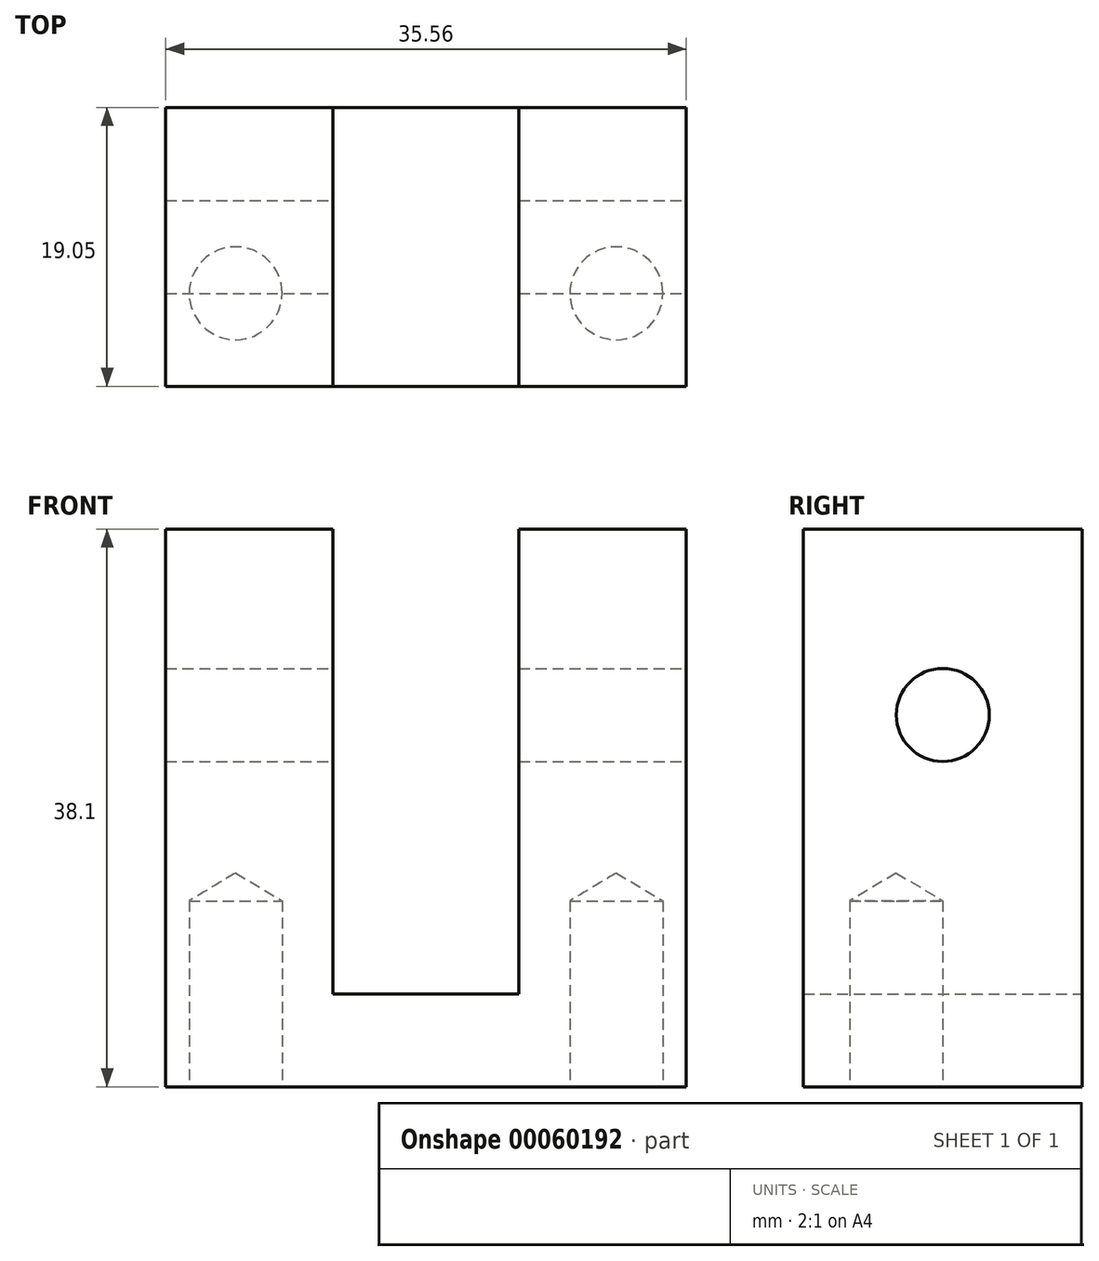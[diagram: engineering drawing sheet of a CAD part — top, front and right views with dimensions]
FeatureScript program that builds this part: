
annotation { "Feature Type Name" : "Feature", "Feature Type Description" : "" }
export const myFeature = defineFeature(function(context is Context, id is Id, definition is map)
    precondition{}
    {
        {
            var Q0;
            Q0=qCreatedBy(makeId("Front.planeOp"),FACE);
            var sketch = newSketch(context, id + "F0", { "sketchPlane" : qUnion([Q0])});
            skLineSegment(sketch, "E0", {"start": v(0, 54.37) * mm, "end": v(0, -36.21) * mm, "construction": true});
            skLineSegment(sketch, "E1", {"start": v(-17.78, -25.4) * mm, "end": v(17.78, -25.4) * mm});
            skLineSegment(sketch, "E2", {"start": v(17.78, -25.4) * mm, "end": v(17.78, 12.7) * mm});
            skLineSegment(sketch, "E3", {"start": v(17.78, 12.7) * mm, "end": v(6.35, 12.7) * mm});
            skLineSegment(sketch, "E4", {"start": v(6.35, 12.7) * mm, "end": v(6.35, -19.05) * mm});
            skLineSegment(sketch, "E5", {"start": v(6.35, -19.05) * mm, "end": v(-6.35, -19.05) * mm});
            skLineSegment(sketch, "E6", {"start": v(-6.35, -19.05) * mm, "end": v(-6.35, 12.7) * mm});
            skLineSegment(sketch, "E7", {"start": v(-6.35, 12.7) * mm, "end": v(-17.78, 12.7) * mm});
            skLineSegment(sketch, "E8", {"start": v(-17.78, 12.7) * mm, "end": v(-17.78, -25.4) * mm});
            skLineSegment(sketch, "E9", {"start": v(-40.6, 0) * mm, "end": v(30.07, 0) * mm, "construction": true});
            skSolve(sketch);
        }
        {
            var Q0;
            Q0 = qSketchRegion(id + "F0", true);
            extrude(context, id + "F1", {"entities" : qUnion([Q0]), "depth" : 19.05 * mm});
        }
        {
            var Q0;
            Q0=makeQuery(id+"F1.opExtrude","SWEPT_FACE",FACE,{"disambiguationData":[OSD([sQuery(id+"F0.wireOp",EDGE,"E1")])]});
            var sketch = newSketch(context, id + "F2", { "sketchPlane" : qUnion([Q0])});
            skCircle(sketch, "E10", {"center": v(-13, 12.7) * mm, "radius": 3.18 * mm});
            skCircle(sketch, "E11", {"center": v(13, 12.7) * mm, "radius": 3.18 * mm});
            skLineSegment(sketch, "E12", {"start": v(-26.21, 12.7) * mm, "end": v(26.87, 12.7) * mm, "construction": true});
            skSolve(sketch);
        }
        {
            var Q0;
            Q0=sQuery(id+"F2.wireOp",VERTEX,"E10.center");
            var Q1;
            Q1=sQuery(id+"F2.wireOp",VERTEX,"E11.center");
            var Q2;
            Q2=makeQuery(id+"F1.opExtrude","SWEPT_BODY",BODY,{"disambiguationData":[OSD([sQuery(id+"F0.wireOp",EDGE,"E1"),sQuery(id+"F0.wireOp",EDGE,"E2"),sQuery(id+"F0.wireOp",EDGE,"E3"),sQuery(id+"F0.wireOp",EDGE,"E4"),sQuery(id+"F0.wireOp",EDGE,"E5"),sQuery(id+"F0.wireOp",EDGE,"E6"),sQuery(id+"F0.wireOp",EDGE,"E7"),sQuery(id+"F0.wireOp",EDGE,"E8")])]});
            hole(context, id + "F3", {"style" : HoleStyle.SIMPLE, "holeDiameter" : 6.35 * mm, "endStyle" : HoleEndStyle.BLIND, "holeDepth" : 12.7 * mm, "locations" : qUnion([Q0, Q1]), "scope" : qUnion([Q2])});
        }
        {
            var Q0;
            Q0=makeQuery(id+"F1.opExtrude","SWEPT_FACE",FACE,{"disambiguationData":[OSD([sQuery(id+"F0.wireOp",EDGE,"E2")])]});
            var sketch = newSketch(context, id + "F4", { "sketchPlane" : qUnion([Q0])});
            skCircle(sketch, "E13", {"center": v(-9.53, 0) * mm, "radius": 3.18 * mm});
            skSolve(sketch);
        }
        {
            var Q0;
            Q0=sQuery(id+"F4.wireOp",VERTEX,"E13.center");
            var Q1;
            Q1=makeQuery(id+"F1.opExtrude","SWEPT_BODY",BODY,{"disambiguationData":[OSD([sQuery(id+"F0.wireOp",EDGE,"E1"),sQuery(id+"F0.wireOp",EDGE,"E2"),sQuery(id+"F0.wireOp",EDGE,"E3"),sQuery(id+"F0.wireOp",EDGE,"E4"),sQuery(id+"F0.wireOp",EDGE,"E5"),sQuery(id+"F0.wireOp",EDGE,"E6"),sQuery(id+"F0.wireOp",EDGE,"E7"),sQuery(id+"F0.wireOp",EDGE,"E8")])]});
            hole(context, id + "F5", {"style" : HoleStyle.SIMPLE, "holeDiameter" : 6.35 * mm, "endStyle" : HoleEndStyle.THROUGH, "locations" : qUnion([Q0]), "scope" : qUnion([Q1])});
        }
    });
